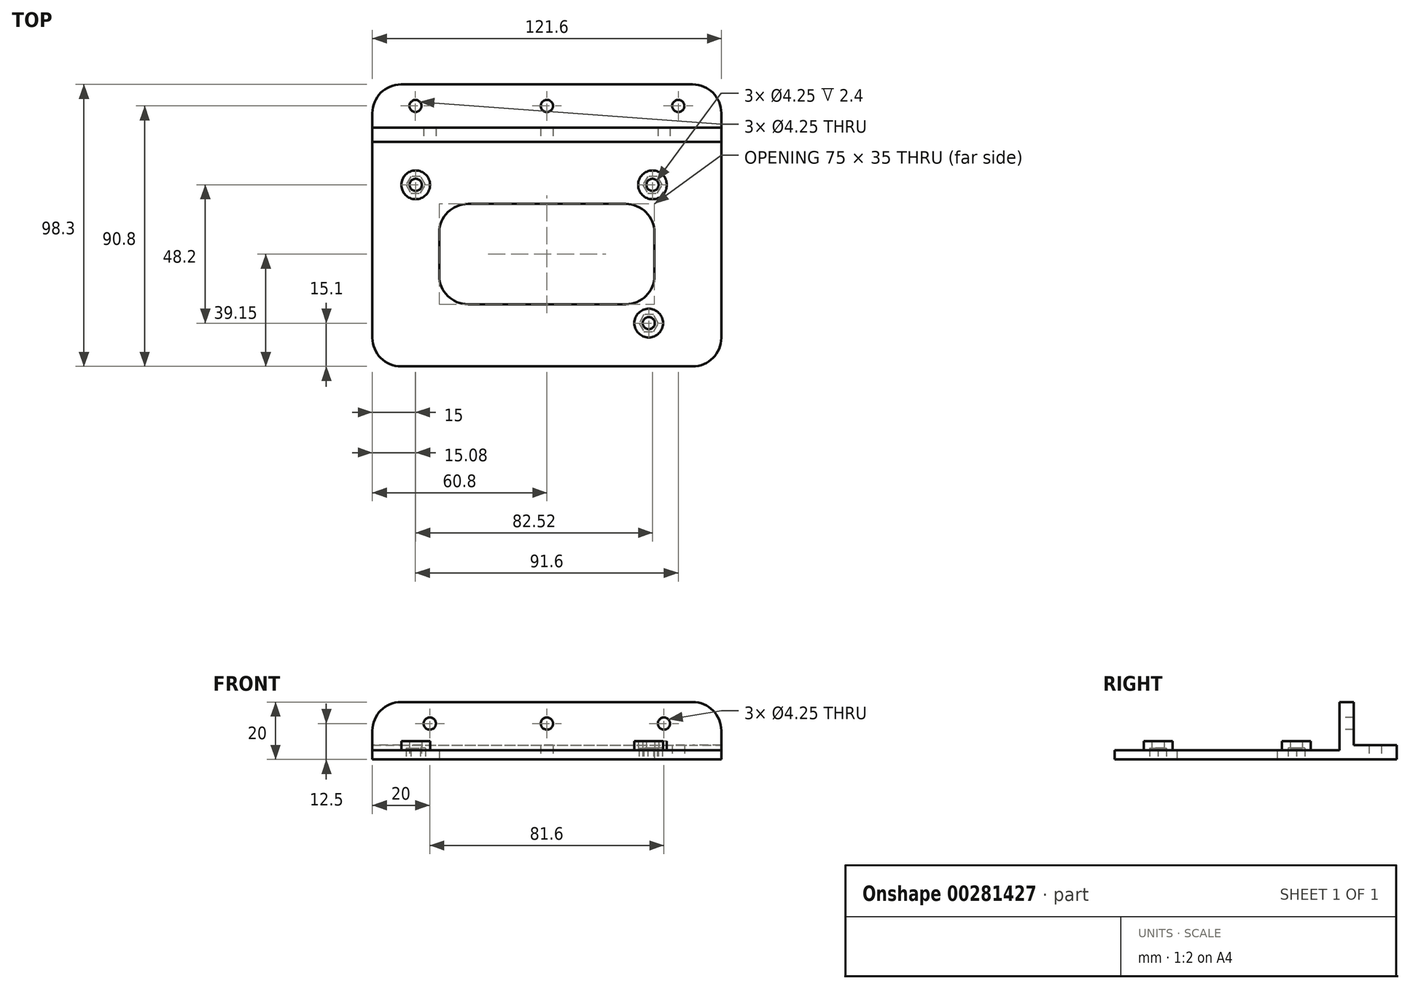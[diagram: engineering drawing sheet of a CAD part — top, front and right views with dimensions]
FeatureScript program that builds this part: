
annotation { "Feature Type Name" : "Feature", "Feature Type Description" : "" }
export const myFeature = defineFeature(function(context is Context, id is Id, definition is map)
    precondition{}
    {
        {
            var Q0;
            Q0=qCreatedBy(makeId("Top.planeOp"),FACE);
            var sketch = newSketch(context, id + "F0", { "sketchPlane" : qUnion([Q0])});
            skLineSegment(sketch, "E0.rect.bottom", {"start": v(50.8, -26.65) * mm, "end": v(-50.8, -26.65) * mm, "construction": true});
            skLineSegment(sketch, "E0.rect.top", {"start": v(50.8, 26.65) * mm, "end": v(-50.8, 26.65) * mm, "construction": true});
            skLineSegment(sketch, "E0.rect.left", {"start": v(50.8, -26.65) * mm, "end": v(50.8, 26.65) * mm, "construction": true});
            skLineSegment(sketch, "E0.rect.right", {"start": v(-50.8, -26.65) * mm, "end": v(-50.8, 26.65) * mm, "construction": true});
            skPoint(sketch, "E0.rect.middle", {"position": v(0, 0) * mm});
            skCircle(sketch, "E1", {"center": v(36.8, 24.15) * mm, "radius": 2.12 * mm});
            skCircle(sketch, "E2", {"center": v(-45.72, 24.15) * mm, "radius": 2.12 * mm});
            skLineSegment(sketch, "E3.rect.bottom", {"start": v(60.8, -39.15) * mm, "end": v(-60.8, -39.15) * mm});
            skLineSegment(sketch, "E3.rect.top", {"start": v(60.8, 39.15) * mm, "end": v(-60.8, 39.15) * mm});
            skLineSegment(sketch, "E3.rect.left", {"start": v(60.8, -39.15) * mm, "end": v(60.8, 39.15) * mm});
            skLineSegment(sketch, "E3.rect.right", {"start": v(-60.8, -39.15) * mm, "end": v(-60.8, 39.15) * mm});
            skLineSegment(sketch, "E4.rect.bottom", {"start": v(27.5, -17.5) * mm, "end": v(-27.5, -17.5) * mm});
            skLineSegment(sketch, "E4.rect.top", {"start": v(27.5, 17.5) * mm, "end": v(-27.5, 17.5) * mm});
            skLineSegment(sketch, "E4.rect.left", {"start": v(37.5, -7.5) * mm, "end": v(37.5, 7.5) * mm});
            skLineSegment(sketch, "E4.rect.right", {"start": v(-37.5, -7.5) * mm, "end": v(-37.5, 7.5) * mm});
            skPoint(sketch, "E5.visualSharp", {"position": v(-37.5, 17.5) * mm});
            skArc(sketch, "E5.filletArc", {"start": v(-27.5, 17.5) * mm, "mid": v(-34.57, 14.57) * mm, "end": v(-37.5, 7.5) * mm});
            skPoint(sketch, "E6.visualSharp", {"position": v(-37.5, -17.5) * mm});
            skArc(sketch, "E6.filletArc", {"start": v(-37.5, -7.5) * mm, "mid": v(-34.57, -14.57) * mm, "end": v(-27.5, -17.5) * mm});
            skPoint(sketch, "E7.visualSharp", {"position": v(37.5, -17.5) * mm});
            skArc(sketch, "E7.filletArc", {"start": v(27.5, -17.5) * mm, "mid": v(34.57, -14.57) * mm, "end": v(37.5, -7.5) * mm});
            skPoint(sketch, "E8.visualSharp", {"position": v(37.5, 17.5) * mm});
            skArc(sketch, "E8.filletArc", {"start": v(37.5, 7.5) * mm, "mid": v(34.57, 14.57) * mm, "end": v(27.5, 17.5) * mm});
            skCircle(sketch, "E9", {"center": v(35.5, -24.05) * mm, "radius": 2.12 * mm});
            skSolve(sketch);
        }
        {
            var Q0;
            Q0=qSketchRegion(id+"F0",true);
            extrude(context, id + "F1", {"entities" : qUnion([Q0]), "depth" : 3.2 * mm});
        }
        {
            var Q0;
            Q0=makeQuery(id+"F1.opExtrude","CAP_FACE",FACE,{"disambiguationData":[OSD([sQuery(id+"F0.wireOp",EDGE,"E1"),sQuery(id+"F0.wireOp",EDGE,"E2"),sQuery(id+"F0.wireOp",EDGE,"427397f8-0dd3-485f-8eed-9c75a59d67ec"),sQuery(id+"F0.wireOp",EDGE,"E3.rect.bottom"),sQuery(id+"F0.wireOp",EDGE,"E3.rect.top"),sQuery(id+"F0.wireOp",EDGE,"E3.rect.left"),sQuery(id+"F0.wireOp",EDGE,"E3.rect.right"),sQuery(id+"F0.wireOp",EDGE,"E4.rect.bottom"),sQuery(id+"F0.wireOp",EDGE,"E4.rect.top"),sQuery(id+"F0.wireOp",EDGE,"E4.rect.left"),sQuery(id+"F0.wireOp",EDGE,"E4.rect.right")])],"isStart":false});
            var sketch = newSketch(context, id + "F2", { "sketchPlane" : qUnion([Q0])});
            skCircle(sketch, "E10", {"center": v(-45.72, 24.15) * mm, "radius": 5 * mm});
            skCircle(sketch, "E11", {"center": v(36.8, 24.15) * mm, "radius": 5 * mm});
            skCircle(sketch, "E12", {"center": v(-45.72, 24.15) * mm, "radius": 2.12 * mm});
            skCircle(sketch, "E13", {"center": v(36.8, 24.15) * mm, "radius": 2.12 * mm});
            skLineSegment(sketch, "E14", {"start": v(0, 0) * mm, "end": v(17.05, 0) * mm, "construction": true});
            skCircle(sketch, "E15", {"center": v(35.5, -24.05) * mm, "radius": 5 * mm});
            skCircle(sketch, "E16", {"center": v(35.5, -24.05) * mm, "radius": 2.12 * mm});
            skSolve(sketch);
        }
        {
            var Q0;
            Q0=qSketchRegion(id+"F2",true);
            extrude(context, id + "F3", {"entities" : qUnion([Q0]), "operationType" : NewBodyOperationType.ADD, "depth" : 3.2 * mm});
        }
        {
            var Q0;
            Q0=makeQuery(id+"F1.opExtrude","CAP_FACE",FACE,{"disambiguationData":[OSD([sQuery(id+"F0.wireOp",EDGE,"E1"),sQuery(id+"F0.wireOp",EDGE,"E2"),sQuery(id+"F0.wireOp",EDGE,"427397f8-0dd3-485f-8eed-9c75a59d67ec"),sQuery(id+"F0.wireOp",EDGE,"E3.rect.bottom"),sQuery(id+"F0.wireOp",EDGE,"E3.rect.top"),sQuery(id+"F0.wireOp",EDGE,"E3.rect.left"),sQuery(id+"F0.wireOp",EDGE,"E3.rect.right"),sQuery(id+"F0.wireOp",EDGE,"E4.rect.bottom"),sQuery(id+"F0.wireOp",EDGE,"E4.rect.top"),sQuery(id+"F0.wireOp",EDGE,"E4.rect.left"),sQuery(id+"F0.wireOp",EDGE,"E4.rect.right")])],"isStart":true});
            var sketch = newSketch(context, id + "F4", { "sketchPlane" : qUnion([Q0])});
            skCircle(sketch, "E17.cCircle", {"center": v(-45.72, -24.15) * mm, "radius": 2.93 * mm, "construction": true});
            skLineSegment(sketch, "E17.0", {"start": v(-47.4, -21.23) * mm, "end": v(-44.03, -21.23) * mm});
            skLineSegment(sketch, "E17.1", {"start": v(-44.03, -21.23) * mm, "end": v(-42.34, -24.15) * mm});
            skLineSegment(sketch, "E17.2", {"start": v(-42.34, -24.15) * mm, "end": v(-44.03, -27.08) * mm});
            skLineSegment(sketch, "E17.3", {"start": v(-44.03, -27.08) * mm, "end": v(-47.4, -27.08) * mm});
            skLineSegment(sketch, "E17.4", {"start": v(-47.4, -27.08) * mm, "end": v(-49.1, -24.15) * mm});
            skLineSegment(sketch, "E17.5", {"start": v(-49.1, -24.15) * mm, "end": v(-47.4, -21.23) * mm});
            skPoint(sketch, "E17.0.midPoint", {"position": v(-45.72, -21.23) * mm});
            skCircle(sketch, "E18.cCircle", {"center": v(36.8, -24.15) * mm, "radius": 2.93 * mm, "construction": true});
            skLineSegment(sketch, "E18.0", {"start": v(35.11, -21.22) * mm, "end": v(38.49, -21.22) * mm});
            skLineSegment(sketch, "E18.1", {"start": v(38.49, -21.22) * mm, "end": v(40.18, -24.15) * mm});
            skLineSegment(sketch, "E18.2", {"start": v(40.18, -24.15) * mm, "end": v(38.49, -27.08) * mm});
            skLineSegment(sketch, "E18.3", {"start": v(38.49, -27.07) * mm, "end": v(35.11, -27.07) * mm});
            skLineSegment(sketch, "E18.4", {"start": v(35.11, -27.08) * mm, "end": v(33.42, -24.15) * mm});
            skLineSegment(sketch, "E18.5", {"start": v(33.42, -24.15) * mm, "end": v(35.11, -21.22) * mm});
            skPoint(sketch, "E18.0.midPoint", {"position": v(36.8, -21.23) * mm});
            skCircle(sketch, "E19.cCircle", {"center": v(35.5, 24.05) * mm, "radius": 2.93 * mm, "construction": true});
            skLineSegment(sketch, "E19.0", {"start": v(37.19, 21.12) * mm, "end": v(33.81, 21.12) * mm});
            skLineSegment(sketch, "E19.1", {"start": v(33.81, 21.12) * mm, "end": v(32.12, 24.05) * mm});
            skLineSegment(sketch, "E19.2", {"start": v(32.12, 24.05) * mm, "end": v(33.81, 26.97) * mm});
            skLineSegment(sketch, "E19.3", {"start": v(33.81, 26.97) * mm, "end": v(37.19, 26.97) * mm});
            skLineSegment(sketch, "E19.4", {"start": v(37.19, 26.97) * mm, "end": v(38.88, 24.05) * mm});
            skLineSegment(sketch, "E19.5", {"start": v(38.88, 24.05) * mm, "end": v(37.19, 21.12) * mm});
            skPoint(sketch, "E19.0.midPoint", {"position": v(35.5, 21.12) * mm});
            skSolve(sketch);
        }
        {
            var Q0;
            Q0=qSketchRegion(id+"F4",true);
            extrude(context, id + "F5", {"entities" : qUnion([Q0]), "operationType" : NewBodyOperationType.REMOVE, "oppositeDirection" : true, "depth" : 4 * mm});
        }
        {
            var Q0;
            Q0=qCreatedBy(makeId("Top.planeOp"),FACE);
            var sketch = newSketch(context, id + "F6", { "sketchPlane" : qUnion([Q0])});
            skLineSegment(sketch, "E20.bottom", {"start": v(-60.8, 39.15) * mm, "end": v(60.8, 39.15) * mm});
            skLineSegment(sketch, "E20.top", {"start": v(-60.8, 59.15) * mm, "end": v(60.8, 59.15) * mm});
            skLineSegment(sketch, "E20.left", {"start": v(-60.8, 39.15) * mm, "end": v(-60.8, 59.15) * mm});
            skLineSegment(sketch, "E20.right", {"start": v(60.8, 39.15) * mm, "end": v(60.8, 59.15) * mm});
            skCircle(sketch, "E21", {"center": v(-45.8, 51.65) * mm, "radius": 2.12 * mm});
            skCircle(sketch, "E22", {"center": v(0, 51.65) * mm, "radius": 2.12 * mm});
            skCircle(sketch, "E23.MirrorC", {"center": v(45.8, 51.65) * mm, "radius": 2.12 * mm});
            skSolve(sketch);
        }
        {
            var Q0;
            Q0=qSketchRegion(id+"F6",true);
            extrude(context, id + "F7", {"entities" : qUnion([Q0]), "operationType" : NewBodyOperationType.ADD, "depth" : 5 * mm});
        }
        {
            var Q0;
            Q0=makeQuery(id+"F7.opExtrude","SWEPT_FACE",FACE,{"disambiguationData":[OSD([sQuery(id+"F6.wireOp",EDGE,"E20.bottom")])]});
            var sketch = newSketch(context, id + "F8", { "sketchPlane" : qUnion([Q0])});
            skLineSegment(sketch, "E24.bottom", {"start": v(-60.8, 5) * mm, "end": v(60.8, 5) * mm});
            skLineSegment(sketch, "E24.top", {"start": v(-60.8, 20) * mm, "end": v(60.8, 20) * mm});
            skLineSegment(sketch, "E24.left", {"start": v(-60.8, 5) * mm, "end": v(-60.8, 20) * mm});
            skLineSegment(sketch, "E24.right", {"start": v(60.8, 5) * mm, "end": v(60.8, 20) * mm});
            skCircle(sketch, "E25", {"center": v(0, 12.5) * mm, "radius": 2.12 * mm});
            skCircle(sketch, "E26", {"center": v(-40.8, 12.5) * mm, "radius": 2.12 * mm});
            skCircle(sketch, "E27.MirrorC", {"center": v(40.8, 12.5) * mm, "radius": 2.12 * mm});
            skSolve(sketch);
        }
        {
            var Q0;
            Q0=qSketchRegion(id+"F8",true);
            extrude(context, id + "F9", {"entities" : qUnion([Q0]), "operationType" : NewBodyOperationType.ADD, "oppositeDirection" : true, "depth" : 5 * mm});
        }
        {
            var Q0;
            Q0=makeQuery(id+"F1.opExtrude","SWEPT_EDGE",EDGE,{"disambiguationData":[OSD([sQuery(id+"F0.wireOp",EDGE,"E3.rect.bottom"),sQuery(id+"F0.wireOp",EDGE,"E3.rect.left")])]});
            var Q1;
            Q1=makeQuery(id+"F1.opExtrude","SWEPT_EDGE",EDGE,{"disambiguationData":[OSD([sQuery(id+"F0.wireOp",EDGE,"E3.rect.bottom"),sQuery(id+"F0.wireOp",EDGE,"E3.rect.right")])]});
            var Q2;
            Q2=makeQuery(id+"F7.opExtrude","SWEPT_EDGE",EDGE,{"disambiguationData":[OSD([sQuery(id+"F6.wireOp",EDGE,"E20.top"),sQuery(id+"F6.wireOp",EDGE,"E20.left")])]});
            var Q3;
            Q3=makeQuery(id+"F9.opExtrude","SWEPT_EDGE",EDGE,{"disambiguationData":[OSD([sQuery(id+"F8.wireOp",EDGE,"E24.top"),sQuery(id+"F8.wireOp",EDGE,"E24.left")])]});
            var Q4;
            Q4=makeQuery(id+"F9.opExtrude","SWEPT_EDGE",EDGE,{"disambiguationData":[OSD([sQuery(id+"F8.wireOp",EDGE,"E24.top"),sQuery(id+"F8.wireOp",EDGE,"E24.right")])]});
            var Q5;
            Q5=makeQuery(id+"F7.opExtrude","SWEPT_EDGE",EDGE,{"disambiguationData":[OSD([sQuery(id+"F6.wireOp",EDGE,"E20.top"),sQuery(id+"F6.wireOp",EDGE,"E20.right")])]});
            fillet(context, id + "F10", {"entities" : qUnion([Q0, Q1, Q2, Q3, Q4, Q5]), "radius" : 10 * mm, "tangentPropagation" : true, "allowEdgeOverflow" : false});
        }
    });
